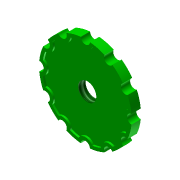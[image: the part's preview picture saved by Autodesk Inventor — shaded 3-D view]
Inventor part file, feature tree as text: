
AUTODESK INVENTOR PART (.ipt)
format: ipt  version: 2012 (Build 160160000, 160)  size: 181,248 bytes
history: native  units: in
note: dims shown in document units (in); Inventor stores cm internally (conversion verified against a paired STEP export)
features: extrude x3, sketch x3, pattern_circular x1, hole x1
ambient origin geometry x8: Origin, YZ Plane, XZ Plane, XY Plane, X Axis, Y Axis, Z Axis, Center Point
bodies: Solid1 (feature_tree)
feature tree (8):
  extrude  "Extrusion1"  Depth=0.1in TaperAngle=0.0deg
  extrude  "Extrusion2"  Depth=0.1in TaperAngle=0.0deg
  pattern_circular  "Circular Pattern1"  Count=12 Angle=360.0deg
  extrude  "Extrusion3"  Depth=0.02in TaperAngle=0.0deg
  hole  "Hole1"  [1 undecoded]
  sketch  "Sketch1"  dims[d9=1.0in d10=0.1in d11=0.0in]
  sketch  "Sketch2"  dims[d12=0.1in d13=0.1in d14=0.0in d15=4.7244in d16=360.0deg]
  sketch  "Sketch3"  dims[d18=0.035in d19=0.02in d20=0.0in d21=1.0in d22=1.0in d23=0.196in d24=0.75in d25=0.375in d26=0.25in d27=0.5635in d28=1.0in d29=0.8108in]
note: 1 required parameter value undecoded (feature->parameter linkage not recoverable at this tier; creation-order binding heuristic only, values carry confidence <= 0.55)
